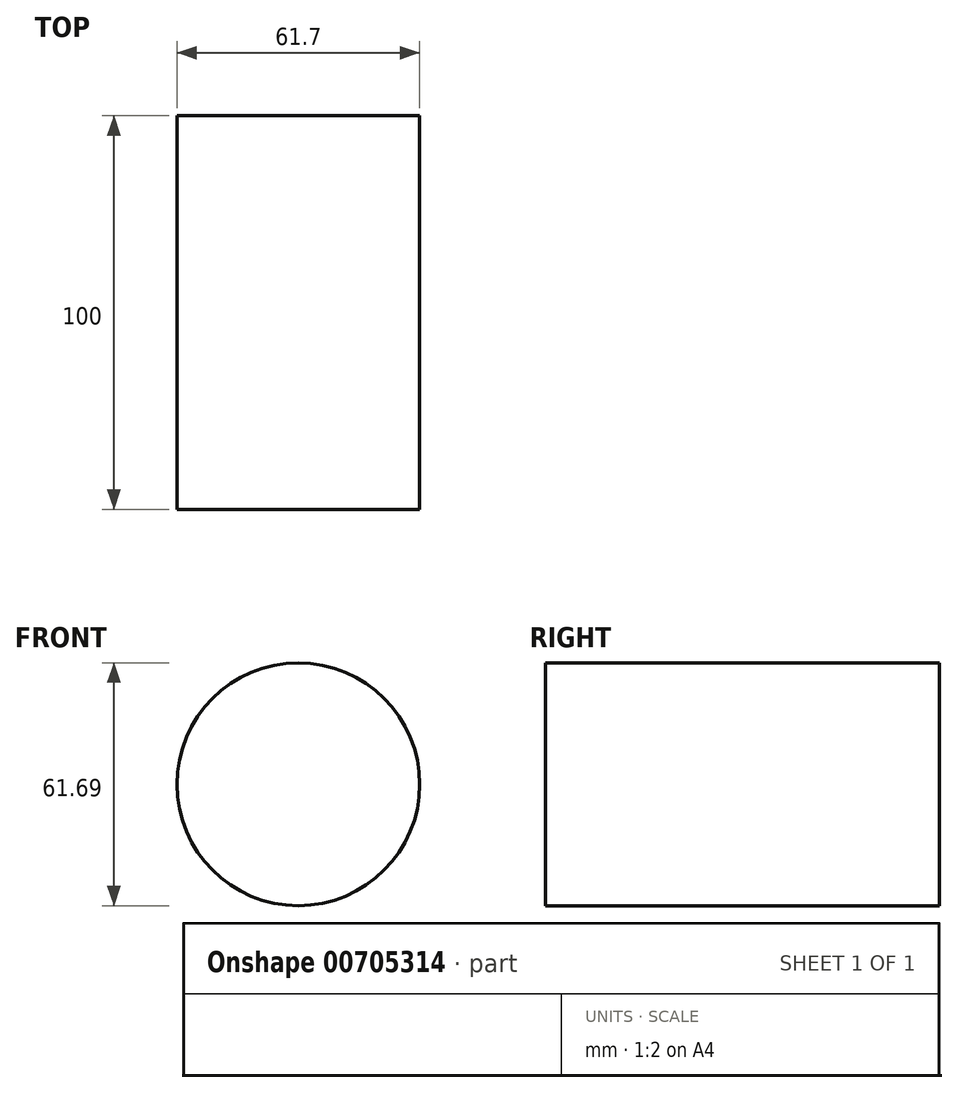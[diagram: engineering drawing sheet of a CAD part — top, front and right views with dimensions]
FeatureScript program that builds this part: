
annotation { "Feature Type Name" : "Feature", "Feature Type Description" : "" }
export const myFeature = defineFeature(function(context is Context, id is Id, definition is map)
    precondition{}
    {
        {
            var Q0;
            Q0=qCreatedBy(makeId("Front.planeOp"),FACE);
            var sketch = newSketch(context, id + "F0", { "sketchPlane" : qUnion([Q0])});
            skCircle(sketch, "E0", {"center": v(-2.45, 2.09) * mm, "radius": 30.85 * mm});
            skSolve(sketch);
        }
        {
            var Q0;
            Q0=makeQuery(id+"F0.imprint","IMPRINT",FACE,{"disambiguationData":[TD([[makeQuery(id+"F0.imprint","IMPRINT",EDGE,{"derivedFrom":sQuery(id+"F0.wireOp",EDGE,"E0")}),1.0]])]});
            var Q1;
            Q1=sQuery(id+"F0.wireOp",EDGE,"E0");
            extrude(context, id + "F1", {"entities" : qUnion([Q0]), "bodyType" : ToolBodyType.SURFACE, "surfaceEntities" : qUnion([Q1]), "depth" : 100 * mm, "offsetDistance" : 25 * mm});
        }
    });
